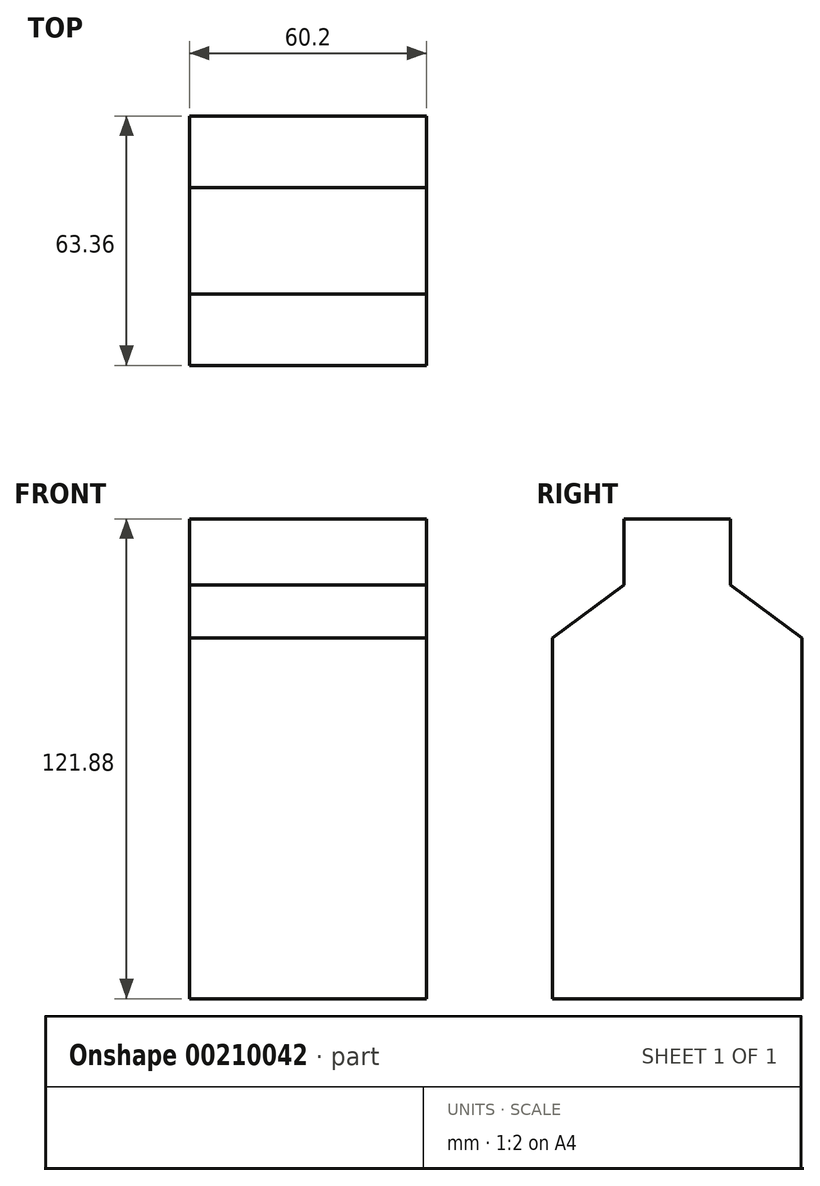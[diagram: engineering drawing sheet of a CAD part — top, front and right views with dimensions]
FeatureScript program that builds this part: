
annotation { "Feature Type Name" : "Feature", "Feature Type Description" : "" }
export const myFeature = defineFeature(function(context is Context, id is Id, definition is map)
    precondition{}
    {
        {
            var Q0;
            Q0=qCreatedBy(makeId("Right.planeOp"),FACE);
            var sketch = newSketch(context, id + "F0", { "sketchPlane" : qUnion([Q0])});
            skLineSegment(sketch, "E0.bottom", {"start": v(-31.68, -54.38) * mm, "end": v(31.68, -54.38) * mm});
            skLineSegment(sketch, "E0.left", {"start": v(-31.68, -54.38) * mm, "end": v(-31.68, 37.23) * mm});
            skLineSegment(sketch, "E0.right", {"start": v(31.68, -54.38) * mm, "end": v(31.68, 37.23) * mm});
            skPoint(sketch, "E0.middle", {"position": v(0, -8.58) * mm});
            skLineSegment(sketch, "E1", {"start": v(31.68, 37.23) * mm, "end": v(13.52, 50.75) * mm});
            skLineSegment(sketch, "E2", {"start": v(13.52, 50.75) * mm, "end": v(13.52, 67.5) * mm});
            skLineSegment(sketch, "E3", {"start": v(13.52, 67.5) * mm, "end": v(0, 67.5) * mm});
            skLineSegment(sketch, "E4.MirrorCS", {"start": v(-13.52, 67.5) * mm, "end": v(0, 67.5) * mm});
            skLineSegment(sketch, "E5.MirrorCS", {"start": v(-13.52, 50.75) * mm, "end": v(-13.52, 67.5) * mm});
            skLineSegment(sketch, "E6.MirrorCS", {"start": v(-31.68, 37.23) * mm, "end": v(-13.52, 50.75) * mm});
            skSolve(sketch);
        }
        {
            var Q0;
            Q0=makeQuery(id+"F0.imprint","IMPRINT",FACE,{"disambiguationData":[TD([[makeQuery(id+"F0.imprint","IMPRINT",EDGE,{"derivedFrom":sQuery(id+"F0.wireOp",EDGE,"E0.bottom")}),1.0]])]});
            extrude(context, id + "F1", {"entities" : qUnion([Q0]), "depth" : 60.2 * mm});
        }
    });
